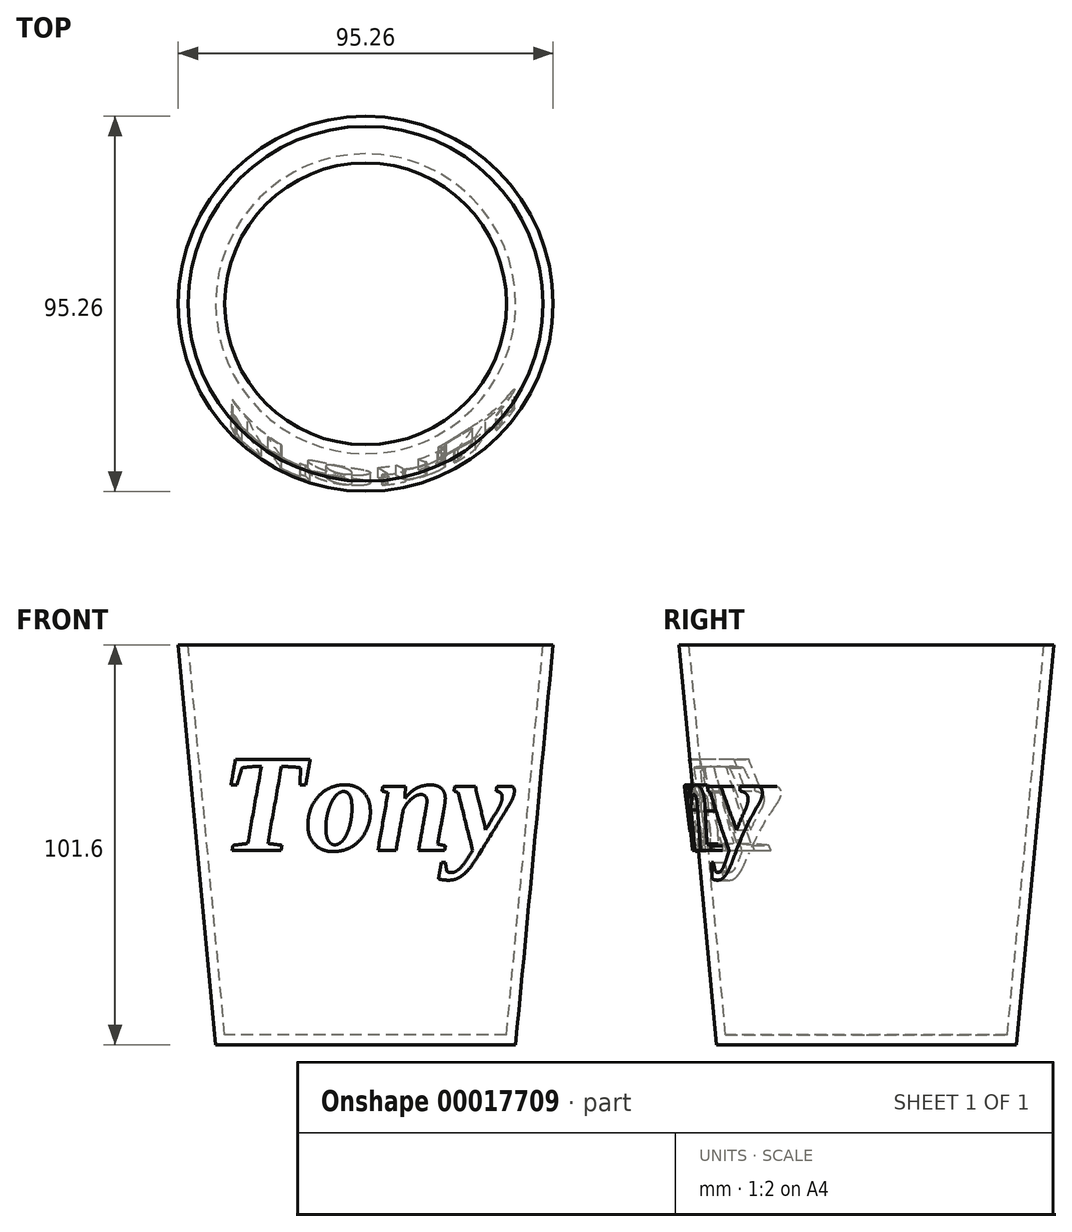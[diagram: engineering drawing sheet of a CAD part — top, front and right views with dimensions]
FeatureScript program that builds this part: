
annotation { "Feature Type Name" : "Feature", "Feature Type Description" : "" }
export const myFeature = defineFeature(function(context is Context, id is Id, definition is map)
    precondition{}
    {
        {
            var Q0;
            Q0=qCreatedBy(makeId("Top.planeOp"),FACE);
            var sketch = newSketch(context, id + "F0", { "sketchPlane" : qUnion([Q0])});
            skCircle(sketch, "E0", {"center": v(0, 0) * mm, "radius": 38.1 * mm});
            skSolve(sketch);
        }
        {
            var Q0;
            Q0=qCreatedBy(makeId("Top.planeOp"),FACE);
            cPlane(context, id + "F1", {"entities" : qUnion([Q0]), "cplaneType" : CPlaneType.OFFSET, "offset" : 101.6 * mm, "width" : 152.4 * mm, "height" : 152.4 * mm});
        }
        {
            var Q0;
            Q0=qCreatedBy(id+"F1.planeOp",FACE);
            var sketch = newSketch(context, id + "F2", { "sketchPlane" : qUnion([Q0])});
            skPoint(sketch, "E1.0", {"position": v(0, 0) * mm});
            skCircle(sketch, "E2", {"center": v(0, 0) * mm, "radius": 50.8 * mm});
            skSolve(sketch);
        }
        {
            var Q0;
            Q0=makeQuery(id+"F0.imprint","IMPRINT",FACE,{"disambiguationData":[TD([[makeQuery(id+"F0.imprint","IMPRINT",EDGE,{"derivedFrom":sQuery(id+"F0.wireOp",EDGE,"E0")}),1.0]])]});
            var Q1;
            Q1=makeQuery(id+"F2.imprint","IMPRINT",FACE,{"disambiguationData":[TD([[makeQuery(id+"F2.imprint","IMPRINT",EDGE,{"derivedFrom":sQuery(id+"F2.wireOp",EDGE,"E2")}),1.0]])]});
            loft(context, id + "F3", {"sheetProfilesArray" : [{ "sheetProfileEntities" : qUnion([Q0]) }, { "sheetProfileEntities" : qUnion([Q1]) }]});
        }
        {
            var Q0;
            Q0=makeQuery(id+"F3.opLoft","CAP_FACE",FACE,{"disambiguationData":[OSD([makeQuery(id+"F2.imprint","IMPRINT",FACE,{"disambiguationData":[TD([[makeQuery(id+"F2.imprint","IMPRINT",EDGE,{"derivedFrom":sQuery(id+"F2.wireOp",EDGE,"E2")}),1.0]])]})])],"isStart":true});
            shell(context, id + "F4", {"entities" : qUnion([Q0]), "thickness" : 2.54 * mm});
        }
        {
            var Q0;
            Q0=qCreatedBy(makeId("Front.planeOp"),FACE);
            var sketch = newSketch(context, id + "F5", { "sketchPlane" : qUnion([Q0])});
            skText(sketch, "E3", { "text": "Tony", "fontName": "Tinos-BoldItalic.ttf"});
            const initialGuessF5  = {"E3": [-0.03678, 0.0494, 1, 0, 0.0254]};
            skSetInitialGuess(sketch, initialGuessF5);
            skSolve(sketch);
        }
        {
            var Q0;
            Q0 = qSketchRegion(id + "F5", true);
            extrude(context, id + "F6", {"entities" : qUnion([Q0]), "operationType" : NewBodyOperationType.INTERSECT, "depth" : 60.58 * mm});
        }
        {
            var Q0;
            Q0=qCreatedBy(makeId("Top.planeOp"),FACE);
            var sketch = newSketch(context, id + "F7", { "sketchPlane" : qUnion([Q0])});
            skCircle(sketch, "E4", {"center": v(0, 0) * mm, "radius": 38.1 * mm});
            skSolve(sketch);
        }
        {
            var Q0;
            Q0=qCreatedBy(id+"F1.planeOp",FACE);
            var sketch = newSketch(context, id + "F8", { "sketchPlane" : qUnion([Q0])});
            skPoint(sketch, "E5.0", {"position": v(0, 0) * mm});
            skCircle(sketch, "E6", {"center": v(0, 0) * mm, "radius": 47.63 * mm});
            skSolve(sketch);
        }
        {
            var Q0;
            Q0=makeQuery(id+"F8.imprint","IMPRINT",FACE,{"disambiguationData":[TD([[makeQuery(id+"F8.imprint","IMPRINT",EDGE,{"derivedFrom":sQuery(id+"F8.wireOp",EDGE,"E6")}),1.0]])]});
            var Q1;
            Q1=makeQuery(id+"F7.imprint","IMPRINT",FACE,{"disambiguationData":[TD([[makeQuery(id+"F7.imprint","IMPRINT",EDGE,{"derivedFrom":sQuery(id+"F7.wireOp",EDGE,"E4")}),1.0]])]});
            loft(context, id + "F9", {"sheetProfilesArray" : [{ "sheetProfileEntities" : qUnion([Q0]) }, { "sheetProfileEntities" : qUnion([Q1]) }]});
        }
        {
            var Q0;
            Q0=makeQuery(id+"F9.opLoft","CAP_FACE",FACE,{"disambiguationData":[OSD([makeQuery(id+"F8.imprint","IMPRINT",FACE,{"disambiguationData":[TD([[makeQuery(id+"F8.imprint","IMPRINT",EDGE,{"derivedFrom":sQuery(id+"F8.wireOp",EDGE,"E6")}),1.0]])]})])],"isStart":true});
            shell(context, id + "F10", {"entities" : qUnion([Q0]), "thickness" : 2.54 * mm});
        }
    });
